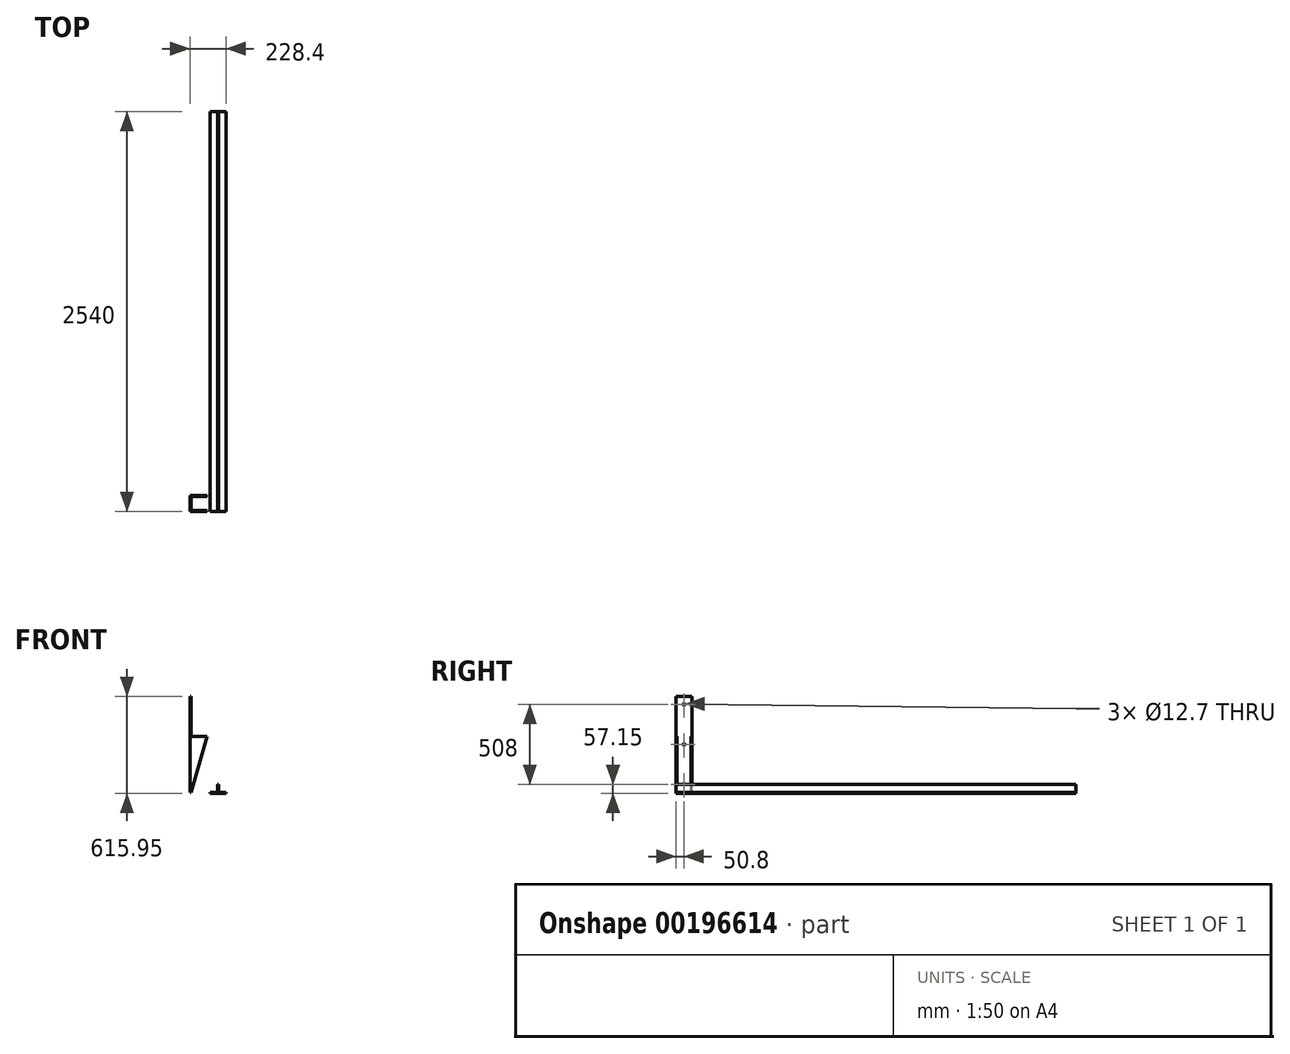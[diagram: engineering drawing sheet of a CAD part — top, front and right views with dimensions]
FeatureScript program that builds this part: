
annotation { "Feature Type Name" : "Feature", "Feature Type Description" : "" }
export const myFeature = defineFeature(function(context is Context, id is Id, definition is map)
    precondition{}
    {
        {
            var Q0;
            Q0=qCreatedBy(makeId("Right.planeOp"),FACE);
            var sketch = newSketch(context, id + "F0", { "sketchPlane" : qUnion([Q0])});
            skLineSegment(sketch, "E0.bottom", {"start": v(0, 0) * mm, "end": v(101.6, 0) * mm});
            skLineSegment(sketch, "E0.top", {"start": v(0, 609.6) * mm, "end": v(101.6, 609.6) * mm});
            skLineSegment(sketch, "E0.left", {"start": v(0, 0) * mm, "end": v(0, 609.6) * mm});
            skLineSegment(sketch, "E0.right", {"start": v(101.6, 0) * mm, "end": v(101.6, 609.6) * mm});
            skCircle(sketch, "E1", {"center": v(50.8, 304.8) * mm, "radius": 6.35 * mm});
            skCircle(sketch, "E2", {"center": v(50.8, 50.8) * mm, "radius": 6.35 * mm});
            skCircle(sketch, "E3", {"center": v(50.8, 558.8) * mm, "radius": 6.35 * mm});
            skSolve(sketch);
        }
        {
            var Q0;
            Q0 = qSketchRegion(id + "F0", true);
            extrude(context, id + "F1", {"entities" : qUnion([Q0]), "oppositeDirection" : true, "depth" : 6.35 * mm});
        }
        {
            var Q0;
            Q0=qCreatedBy(makeId("Front.planeOp"),FACE);
            var sketch = newSketch(context, id + "F2", { "sketchPlane" : qUnion([Q0])});
            skLineSegment(sketch, "E4", {"start": v(0, 0) * mm, "end": v(101.6, 355.6) * mm});
            skLineSegment(sketch, "E5", {"start": v(101.6, 355.6) * mm, "end": v(0, 355.6) * mm});
            skLineSegment(sketch, "E6", {"start": v(0, 355.6) * mm, "end": v(0, 0) * mm});
            skSolve(sketch);
        }
        {
            var Q0;
            Q0=makeQuery(id+"F2.imprint","IMPRINT",FACE,{"disambiguationData":[TD([[makeQuery(id+"F2.imprint","IMPRINT",EDGE,{"derivedFrom":sQuery(id+"F2.wireOp",EDGE,"E4")}),1.0]])]});
            extrude(context, id + "F3", {"entities" : qUnion([Q0]), "operationType" : NewBodyOperationType.ADD, "oppositeDirection" : true, "depth" : 6.35 * mm});
        }
        {
            var Q0;
            Q0=makeQuery(id+"F1.opExtrude","SWEPT_FACE",FACE,{"disambiguationData":[OSD([sQuery(id+"F0.wireOp",EDGE,"E0.right")])]});
            var sketch = newSketch(context, id + "F4", { "sketchPlane" : qUnion([Q0])});
            skLineSegment(sketch, "E7", {"start": v(0, 0) * mm, "end": v(-101.6, 355.6) * mm});
            skLineSegment(sketch, "E8", {"start": v(-101.6, 355.6) * mm, "end": v(0, 355.6) * mm});
            skLineSegment(sketch, "E9", {"start": v(0, 355.6) * mm, "end": v(0, 0) * mm});
            skSolve(sketch);
        }
        {
            var Q0;
            Q0 = qSketchRegion(id + "F4", true);
            extrude(context, id + "F5", {"entities" : qUnion([Q0]), "operationType" : NewBodyOperationType.ADD, "oppositeDirection" : true, "depth" : 6.35 * mm});
        }
        {
            var Q0;
            Q0=qCreatedBy(makeId("Front.planeOp"),FACE);
            var sketch = newSketch(context, id + "F6", { "sketchPlane" : qUnion([Q0])});
            skLineSegment(sketch, "E10", {"start": v(168.08, 0) * mm, "end": v(168.08, 50.8) * mm});
            skLineSegment(sketch, "E11", {"start": v(168.08, 50.8) * mm, "end": v(174.43, 50.8) * mm});
            skLineSegment(sketch, "E12", {"start": v(174.43, 50.8) * mm, "end": v(174.43, 0) * mm});
            skLineSegment(sketch, "E13", {"start": v(174.43, 0) * mm, "end": v(222.05, 0) * mm});
            skLineSegment(sketch, "E14", {"start": v(222.05, 0) * mm, "end": v(222.05, -6.35) * mm});
            skLineSegment(sketch, "E15", {"start": v(222.05, -6.35) * mm, "end": v(120.45, -6.35) * mm});
            skLineSegment(sketch, "E16", {"start": v(120.45, -6.35) * mm, "end": v(120.45, 0) * mm});
            skLineSegment(sketch, "E17", {"start": v(120.45, 0) * mm, "end": v(168.08, 0) * mm});
            skSolve(sketch);
        }
        {
            var Q0;
            Q0=makeQuery(id+"F6.imprint","IMPRINT",FACE,{"disambiguationData":[TD([[makeQuery(id+"F6.imprint","IMPRINT",EDGE,{"derivedFrom":sQuery(id+"F6.wireOp",EDGE,"E10")}),-1.0]])]});
            extrude(context, id + "F7", {"entities" : qUnion([Q0]), "oppositeDirection" : true, "depth" : 2540 * mm});
        }
    });
